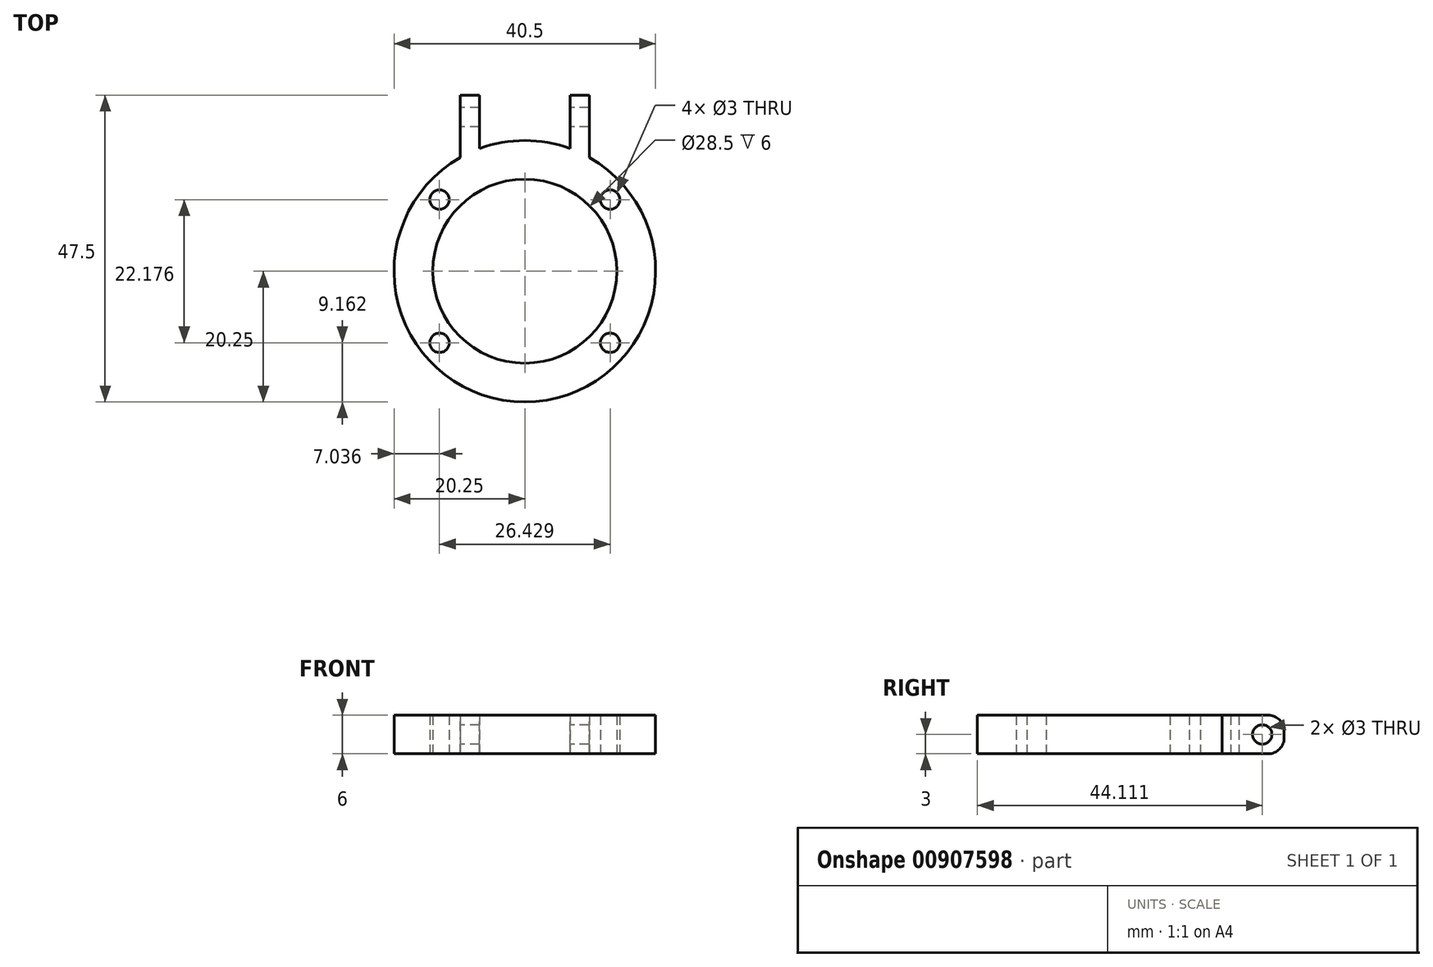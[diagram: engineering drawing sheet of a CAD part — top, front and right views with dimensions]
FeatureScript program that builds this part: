
annotation { "Feature Type Name" : "Feature", "Feature Type Description" : "" }
export const myFeature = defineFeature(function(context is Context, id is Id, definition is map)
    precondition{}
    {
        {
            var Q0;
            Q0=qCreatedBy(makeId("Top.planeOp"),FACE);
            var sketch = newSketch(context, id + "F0", { "sketchPlane" : qUnion([Q0])});
            skCircle(sketch, "E0", {"center": v(0, 0) * mm, "radius": 14.25 * mm});
            skCircle(sketch, "E1.0", {"center": v(0, 0) * mm, "radius": 20.25 * mm});
            skLineSegment(sketch, "E2", {"start": v(-12.07, 10.12) * mm, "end": v(-14.36, 12.05) * mm});
            skLineSegment(sketch, "E3", {"start": v(12.07, 10.12) * mm, "end": v(14.36, 12.05) * mm});
            skCircle(sketch, "E4", {"center": v(-13.21, 11.09) * mm, "radius": 1.5 * mm});
            skCircle(sketch, "E5", {"center": v(13.21, 11.09) * mm, "radius": 1.5 * mm});
            skLineSegment(sketch, "E6", {"start": v(0, 20.25) * mm, "end": v(0, 27.25) * mm, "construction": true});
            skLineSegment(sketch, "E7", {"start": v(0, 27.25) * mm, "end": v(7, 27.25) * mm, "construction": true});
            skLineSegment(sketch, "E8", {"start": v(7, 27.25) * mm, "end": v(7, 19) * mm});
            skLineSegment(sketch, "E9", {"start": v(7, 27.25) * mm, "end": v(10, 27.25) * mm});
            skLineSegment(sketch, "E10", {"start": v(10, 27.25) * mm, "end": v(10, 17.6) * mm});
            skLineSegment(sketch, "E11.MirrorCS", {"start": v(-10, 27.25) * mm, "end": v(-10, 17.6) * mm});
            skLineSegment(sketch, "E12.MirrorCS", {"start": v(-7, 27.25) * mm, "end": v(-10, 27.25) * mm});
            skLineSegment(sketch, "E13.MirrorCS", {"start": v(-7, 27.25) * mm, "end": v(-7, 19) * mm});
            skCircle(sketch, "E14.MirrorC", {"center": v(13.21, -11.09) * mm, "radius": 1.5 * mm});
            skCircle(sketch, "E15.MirrorC", {"center": v(-13.21, -11.09) * mm, "radius": 1.5 * mm});
            skSolve(sketch);
        }
        {
            var Q0;
            Q0 = qSketchRegion(id + "F0", true);
            extrude(context, id + "F1", {"entities" : qUnion([Q0]), "depth" : 6 * mm, "offsetDistance" : 25 * mm});
        }
        {
            var Q0;
            Q0=makeQuery(id+"F1.opExtrude","SWEPT_FACE",FACE,{"disambiguationData":[OSD([sQuery(id+"F0.wireOp",EDGE,"E11.MirrorCS")])]});
            var sketch = newSketch(context, id + "F2", { "sketchPlane" : qUnion([Q0])});
            skCircle(sketch, "E16", {"center": v(-23.86, 3) * mm, "radius": 1.5 * mm});
            skPoint(sketch, "E16.centerSnap0", {"position": v(-27.25, 3) * mm});
            skSolve(sketch);
        }
        {
            var Q0;
            Q0 = qSketchRegion(id + "F2", true);
            extrude(context, id + "F3", {"entities" : qUnion([Q0]), "operationType" : NewBodyOperationType.REMOVE, "endBound" : BoundingType.THROUGH_ALL, "oppositeDirection" : true, "depth" : 25 * mm, "offsetDistance" : 25 * mm});
        }
        {
            var Q0;
            Q0=makeQuery(id+"F1.opExtrude","CAP_EDGE",EDGE,{"disambiguationData":[OSD([sQuery(id+"F0.wireOp",EDGE,"E9")])],"isStart":false});
            var Q1;
            Q1=makeQuery(id+"F1.opExtrude","CAP_EDGE",EDGE,{"disambiguationData":[OSD([sQuery(id+"F0.wireOp",EDGE,"E9")])],"isStart":true});
            var Q2;
            Q2=makeQuery(id+"F1.opExtrude","CAP_EDGE",EDGE,{"disambiguationData":[OSD([sQuery(id+"F0.wireOp",EDGE,"E12.MirrorCS")])],"isStart":true});
            var Q3;
            Q3=makeQuery(id+"F1.opExtrude","CAP_EDGE",EDGE,{"disambiguationData":[OSD([sQuery(id+"F0.wireOp",EDGE,"E12.MirrorCS")])],"isStart":false});
            fillet(context, id + "F4", {"entities" : qUnion([Q0, Q1, Q2, Q3]), "radius" : 2.5 * mm, "tangentPropagation" : true, "allowEdgeOverflow" : false});
        }
    });
